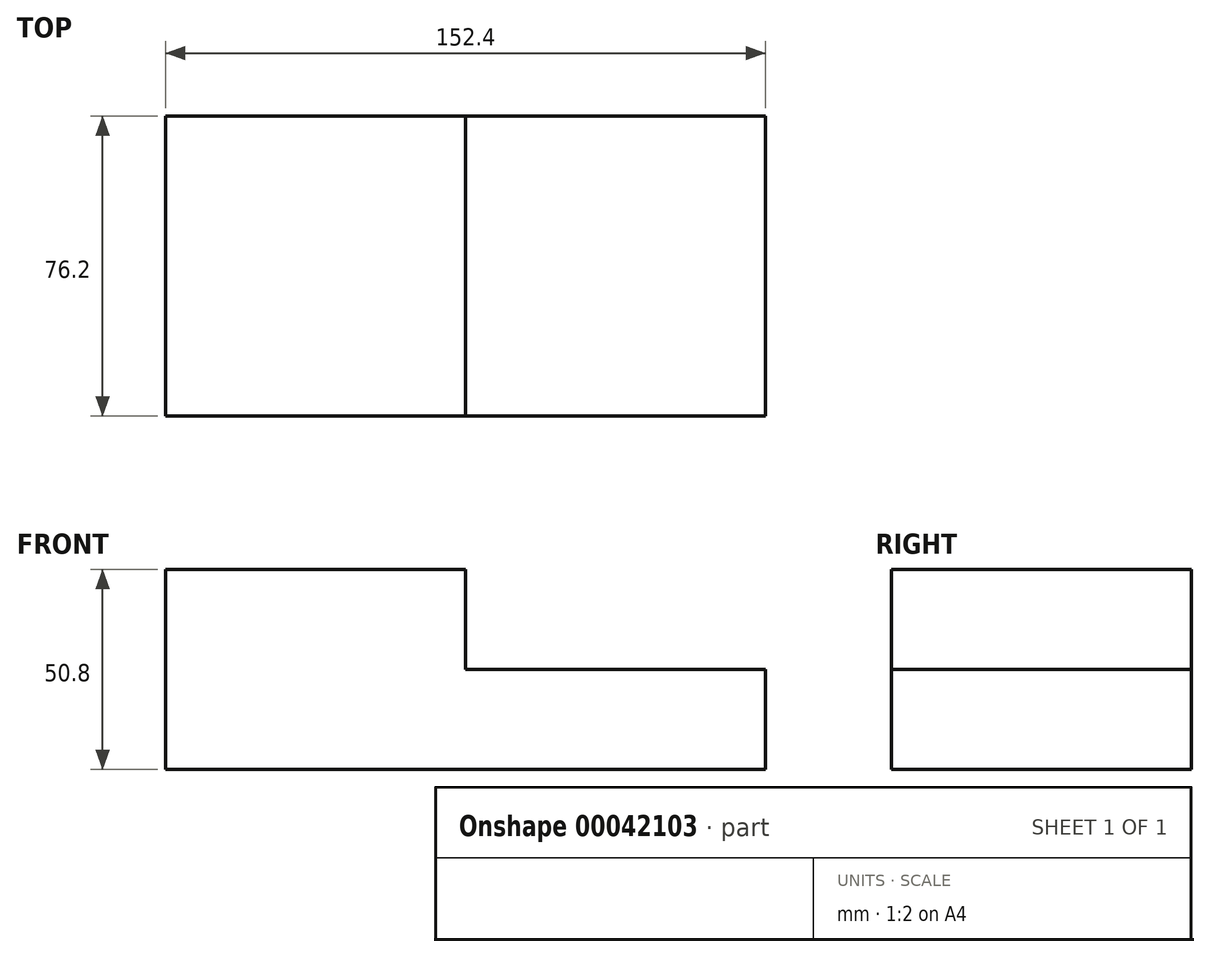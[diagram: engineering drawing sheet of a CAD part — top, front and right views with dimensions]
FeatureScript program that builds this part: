
annotation { "Feature Type Name" : "Feature", "Feature Type Description" : "" }
export const myFeature = defineFeature(function(context is Context, id is Id, definition is map)
    precondition{}
    {
        {
            var Q0;
            Q0=qCreatedBy(makeId("Front.planeOp"),FACE);
            var sketch = newSketch(context, id + "F0", { "sketchPlane" : qUnion([Q0])});
            skLineSegment(sketch, "E0", {"start": v(-76.16, 0) * mm, "end": v(0, 0) * mm});
            skSolve(sketch);
        }
        {
            var Q0;
            Q0=sQuery(id+"F0.wireOp",EDGE,"E0");
            extrude(context, id + "F1", {"bodyType" : ToolBodyType.SURFACE, "surfaceEntities" : qUnion([Q0]), "oppositeDirection" : true, "depth" : 76.2 * mm});
        }
        {
            var Q0;
            Q0=makeQuery(id+"F1.opExtrude","SWEPT_FACE",FACE,{"disambiguationData":[OSD([sQuery(id+"F0.wireOp",EDGE,"E0")])]});
            extrude(context, id + "F2", {"entities" : qUnion([Q0]), "depth" : 50.8 * mm});
        }
        {
            var Q0;
            Q0=makeQuery(id+"F2.opExtrude","SWEPT_FACE",FACE,{"disambiguationData":[OSD([sQuery(id+"F0.wireOp",VERTEX,"E0.end")])]});
            extrude(context, id + "F3", {"entities" : qUnion([Q0]), "operationType" : NewBodyOperationType.ADD, "depth" : 0.04 * mm});
        }
        {
            var Q0;
            Q0=makeQuery(id+"F3.opExtrude","CAP_FACE",FACE,{"disambiguationData":[OSD([sQuery(id+"F0.wireOp",VERTEX,"E0.end")])],"isStart":false});
            var sketch = newSketch(context, id + "F4", { "sketchPlane" : qUnion([Q0])});
            skLineSegment(sketch, "E1", {"start": v(0, 0) * mm, "end": v(0, 25.4) * mm});
            skLineSegment(sketch, "E2", {"start": v(76.2, 0) * mm, "end": v(76.2, 25.4) * mm});
            skLineSegment(sketch, "E3", {"start": v(76.2, 25.4) * mm, "end": v(0, 25.4) * mm});
            skLineSegment(sketch, "E4", {"start": v(0, 0) * mm, "end": v(76.2, 0) * mm});
            skSolve(sketch);
        }
        {
            var Q0;
            Q0=makeQuery(id+"F4.imprint","IMPRINT",FACE,{"disambiguationData":[TD([[makeQuery(id+"F4.imprint","IMPRINT",EDGE,{"derivedFrom":sQuery(id+"F4.wireOp",EDGE,"E1")}),1.0]])]});
            extrude(context, id + "F5", {"entities" : qUnion([Q0]), "operationType" : NewBodyOperationType.ADD, "depth" : 76.2 * mm});
        }
    });
